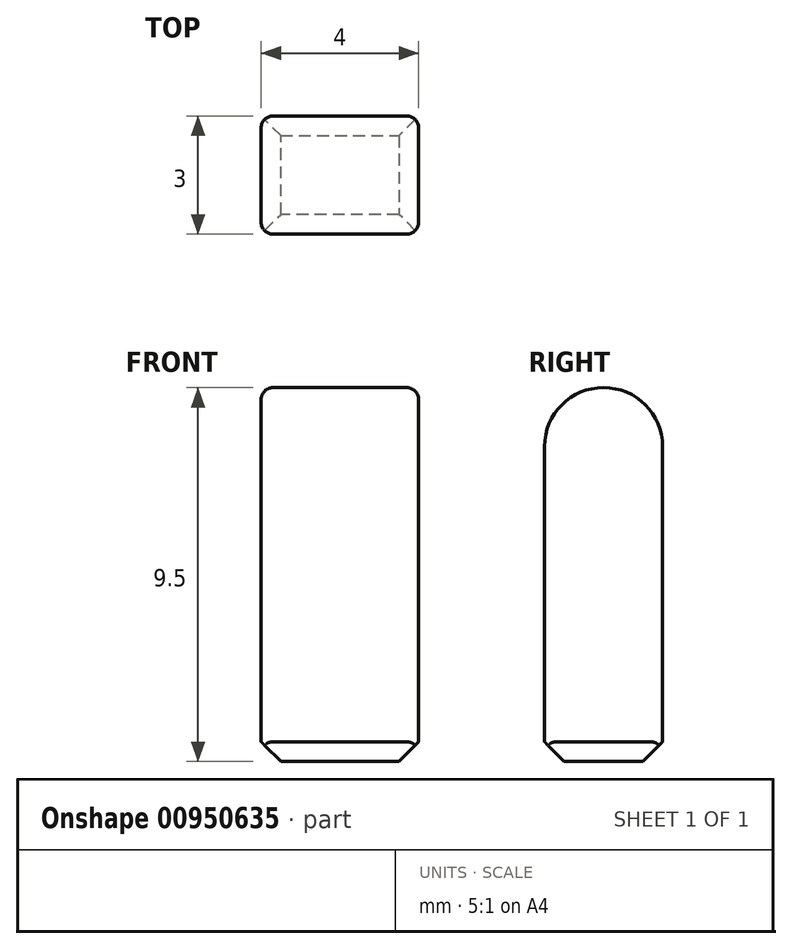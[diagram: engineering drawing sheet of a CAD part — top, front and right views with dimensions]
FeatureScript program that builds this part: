
annotation { "Feature Type Name" : "Feature", "Feature Type Description" : "" }
export const myFeature = defineFeature(function(context is Context, id is Id, definition is map)
    precondition{}
    {
        {
            var Q0;
            Q0=qCreatedBy(makeId("Right.planeOp"),FACE);
            var sketch = newSketch(context, id + "F0", { "sketchPlane" : qUnion([Q0])});
            skLineSegment(sketch, "E0.top", {"start": v(0, -8) * mm, "end": v(3, -8) * mm});
            skLineSegment(sketch, "E0.left", {"start": v(0, 0) * mm, "end": v(0, -8) * mm});
            skLineSegment(sketch, "E0.right", {"start": v(3, 0) * mm, "end": v(3, -8) * mm});
            skArc(sketch, "E1", {"start": v(3, 0) * mm, "mid": v(1.5, 1.5) * mm, "end": v(0, 0) * mm});
            skSolve(sketch);
        }
        {
            var Q0;
            Q0=makeQuery(id+"F0.imprint","IMPRINT",FACE,{"disambiguationData":[TD([[makeQuery(id+"F0.imprint","IMPRINT",EDGE,{"derivedFrom":sQuery(id+"F0.wireOp",EDGE,"E0.top")}),1.0]])]});
            extrude(context, id + "F1", {"entities" : qUnion([Q0]), "depth" : 4 * mm, "offsetDistance" : 25 * mm});
        }
        {
            var Q0;
            Q0=makeQuery(id+"F1.opExtrude","SWEPT_FACE",FACE,{"disambiguationData":[OSD([sQuery(id+"F0.wireOp",EDGE,"E0.top")])]});
            chamfer(context, id + "F2", {"entities" : qUnion([Q0]), "width" : .5 * mm, "tangentPropagation" : true});
        }
        {
            var Q0;
            Q0=makeQuery(id+"F1.opExtrude","CAP_EDGE",EDGE,{"disambiguationData":[OSD([sQuery(id+"F0.wireOp",EDGE,"E0.right")])],"isStart":true});
            var Q1;
            Q1=makeQuery(id+"F1.opExtrude","CAP_EDGE",EDGE,{"disambiguationData":[OSD([sQuery(id+"F0.wireOp",EDGE,"E1")])],"isStart":true});
            var Q2;
            Q2=makeQuery(id+"F1.opExtrude","CAP_EDGE",EDGE,{"disambiguationData":[OSD([sQuery(id+"F0.wireOp",EDGE,"E0.left")])],"isStart":true});
            var Q3;
            Q3=makeQuery(id+"F1.opExtrude","CAP_EDGE",EDGE,{"disambiguationData":[OSD([sQuery(id+"F0.wireOp",EDGE,"E0.right")])],"isStart":false});
            var Q4;
            Q4=makeQuery(id+"F1.opExtrude","CAP_EDGE",EDGE,{"disambiguationData":[OSD([sQuery(id+"F0.wireOp",EDGE,"E1")])],"isStart":false});
            fillet(context, id + "F3", {"entities" : qUnion([Q0, Q1, Q2, Q3, Q4]), "radius" : .3 * mm, "tangentPropagation" : true, "allowEdgeOverflow" : false});
        }
    });
